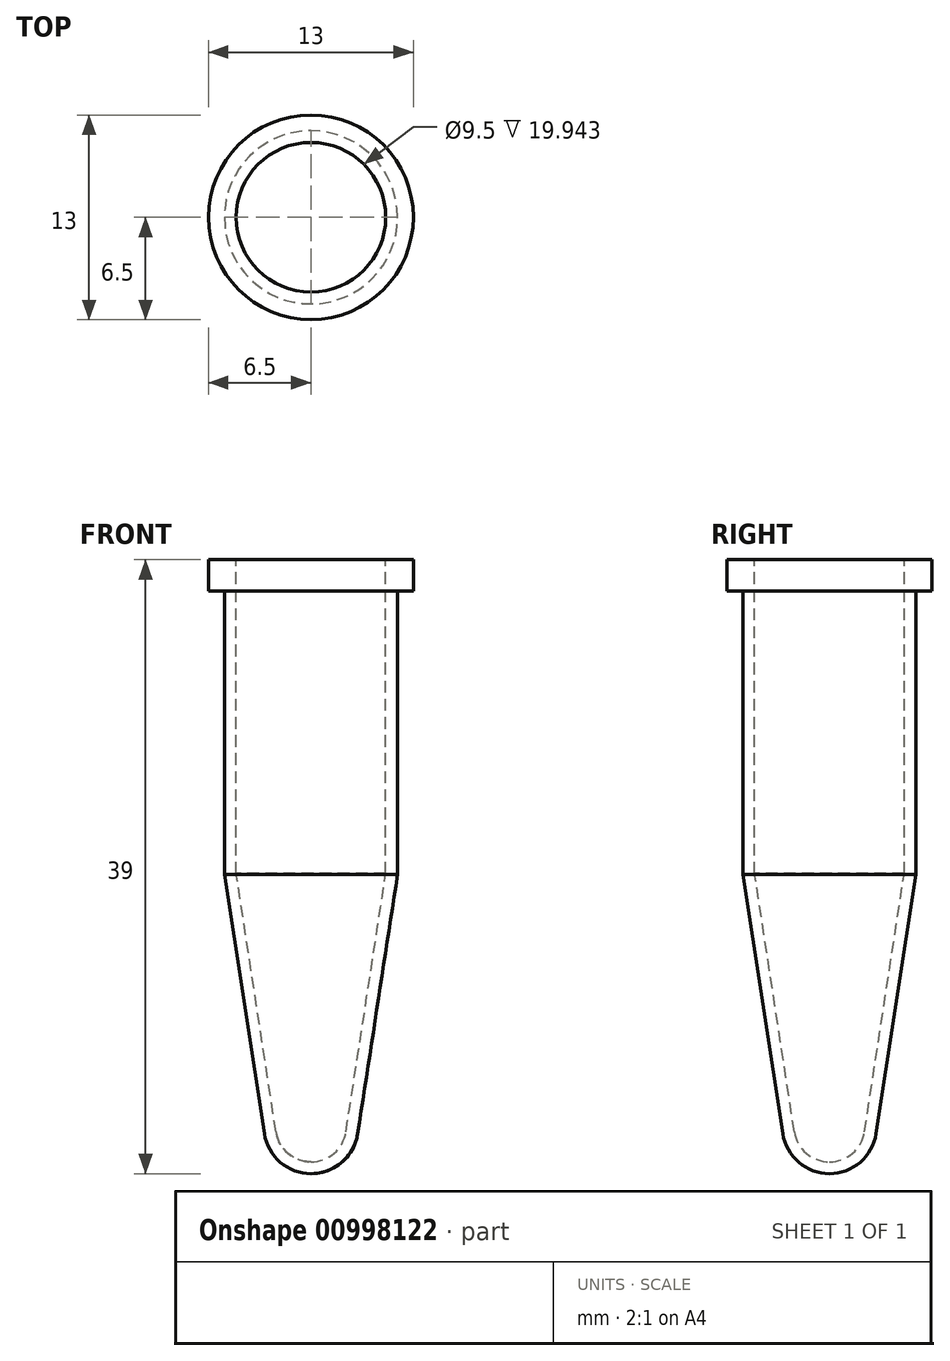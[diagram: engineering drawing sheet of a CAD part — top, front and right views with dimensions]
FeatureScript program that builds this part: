
annotation { "Feature Type Name" : "Feature", "Feature Type Description" : "" }
export const myFeature = defineFeature(function(context is Context, id is Id, definition is map)
    precondition{}
    {
        {
            var Q0;
            Q0=qCreatedBy(makeId("Front.planeOp"),FACE);
            var sketch = newSketch(context, id + "F0", { "sketchPlane" : qUnion([Q0])});
            skLineSegment(sketch, "E0", {"start": v(0, 0) * mm, "end": v(0, -39) * mm, "construction": true});
            skArc(sketch, "E1", {"start": v(0, -39) * mm, "mid": v(1.95, -38.28) * mm, "end": v(2.97, -36.46) * mm});
            skLineSegment(sketch, "E2", {"start": v(2.97, -36.46) * mm, "end": v(5.5, -20) * mm});
            skLineSegment(sketch, "E3", {"start": v(5.5, -20) * mm, "end": v(5.5, -2) * mm});
            skLineSegment(sketch, "E4", {"start": v(5.5, -2) * mm, "end": v(6.5, -2) * mm});
            skLineSegment(sketch, "E5", {"start": v(6.5, -2) * mm, "end": v(6.5, 0) * mm});
            skLineSegment(sketch, "E6", {"start": v(6.5, 0) * mm, "end": v(4.75, 0) * mm});
            skLineSegment(sketch, "E7.0", {"start": v(4.75, -19.94) * mm, "end": v(4.75, 0) * mm});
            skLineSegment(sketch, "E7.1", {"start": v(2.22, -36.34) * mm, "end": v(4.75, -19.94) * mm});
            skArc(sketch, "E7.2", {"start": v(0, -38.25) * mm, "mid": v(1.46, -37.7) * mm, "end": v(2.22, -36.34) * mm});
            skLineSegment(sketch, "E8", {"start": v(4.75, 0) * mm, "end": v(4.75, 0) * mm});
            skLineSegment(sketch, "E9", {"start": v(0, -38.25) * mm, "end": v(0, -39) * mm});
            skSolve(sketch);
        }
        {
            var Q0;
            Q0 = qSketchRegion(id + "F0", true);
            var Q1;
            Q1=sQuery(id+"F0.wireOp",EDGE,"E0");
            revolve(context, id + "F1", {"surfaceOperationType" : NewSurfaceOperationType.NEW, "entities" : qUnion([Q0]), "axis" : qUnion([Q1]), "revolveType" : RevolveType.FULL});
        }
    });
